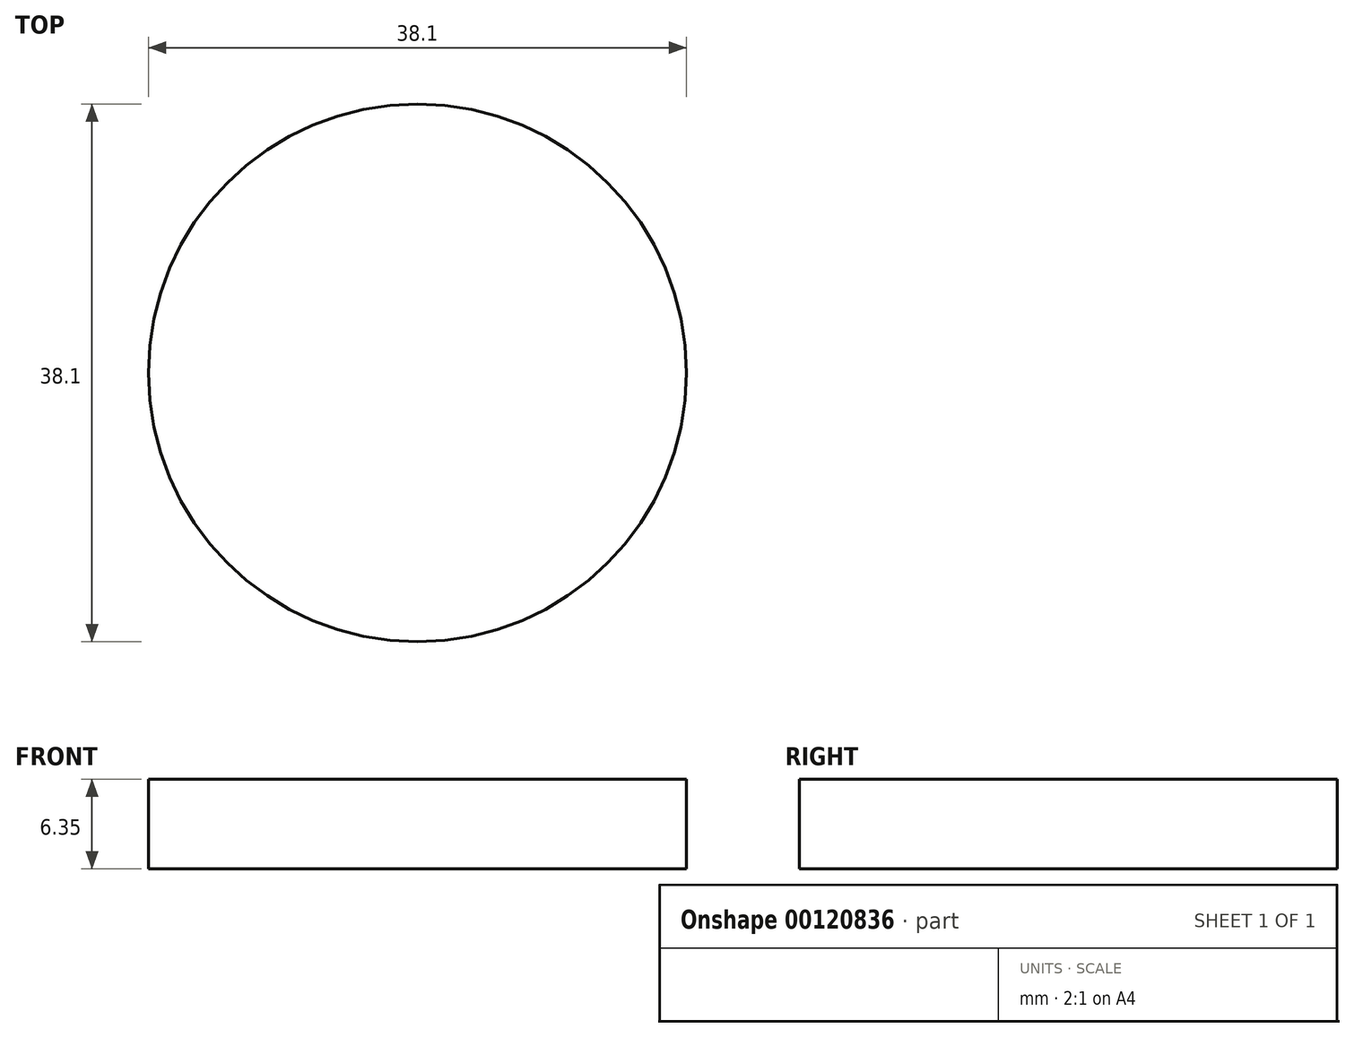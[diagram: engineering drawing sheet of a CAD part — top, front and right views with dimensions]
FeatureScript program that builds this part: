
annotation { "Feature Type Name" : "Feature", "Feature Type Description" : "" }
export const myFeature = defineFeature(function(context is Context, id is Id, definition is map)
    precondition{}
    {
        {
            var Q0;
            Q0=qCreatedBy(makeId("Top.planeOp"),FACE);
            var sketch = newSketch(context, id + "F0", { "sketchPlane" : qUnion([Q0])});
            skCircle(sketch, "E0", {"center": v(0, 0) * mm, "radius": 19.05 * mm});
            skSolve(sketch);
        }
        {
            var Q0;
            Q0 = qSketchRegion(id + "F0", true);
            extrude(context, id + "F1", {"entities" : qUnion([Q0]), "depth" : 6.35 * mm});
        }
    });
